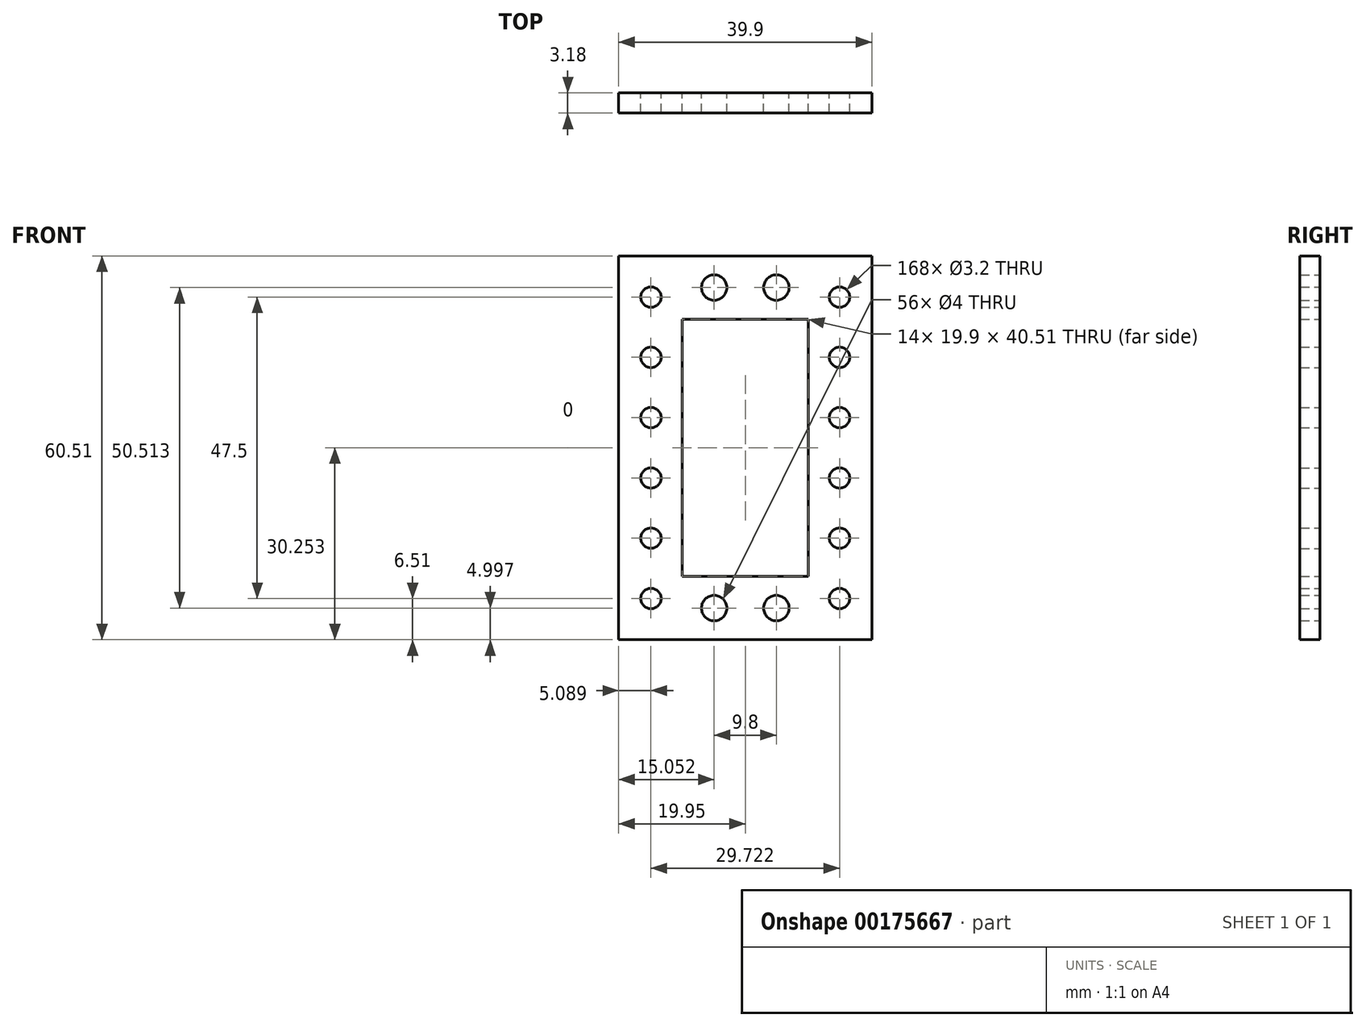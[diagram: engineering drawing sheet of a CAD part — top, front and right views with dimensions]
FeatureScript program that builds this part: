
annotation { "Feature Type Name" : "Feature", "Feature Type Description" : "" }
export const myFeature = defineFeature(function(context is Context, id is Id, definition is map)
    precondition{}
    {
        {
            var Q0;
            Q0=qCreatedBy(makeId("Front.planeOp"),FACE);
            var sketch = newSketch(context, id + "F0", { "sketchPlane" : qUnion([Q0])});
            skLineSegment(sketch, "E0.bottom", {"start": v(0, 0) * mm, "end": v(19.9, 0) * mm});
            skLineSegment(sketch, "E0.top", {"start": v(0, -40.51) * mm, "end": v(19.9, -40.51) * mm});
            skLineSegment(sketch, "E0.left", {"start": v(0, 0) * mm, "end": v(0, -40.51) * mm});
            skLineSegment(sketch, "E0.right", {"start": v(19.9, 0) * mm, "end": v(19.9, -40.51) * mm});
            skLineSegment(sketch, "E1.bottom", {"start": v(-10, 10) * mm, "end": v(29.9, 10) * mm});
            skLineSegment(sketch, "E1.top", {"start": v(-10, -50.51) * mm, "end": v(29.9, -50.51) * mm});
            skLineSegment(sketch, "E1.left", {"start": v(-10, 10) * mm, "end": v(-10, -50.51) * mm});
            skLineSegment(sketch, "E1.right", {"start": v(29.9, 10) * mm, "end": v(29.9, -50.51) * mm});
            skCircle(sketch, "E2", {"center": v(5.05, 5) * mm, "radius": 2 * mm});
            skCircle(sketch, "E3", {"center": v(14.85, 5) * mm, "radius": 2 * mm});
            skCircle(sketch, "E4.MirrorC", {"center": v(5.05, -45.51) * mm, "radius": 2 * mm});
            skCircle(sketch, "E5.MirrorC", {"center": v(14.85, -45.51) * mm, "radius": 2 * mm});
            skCircle(sketch, "E6", {"center": v(-4.91, 3.5) * mm, "radius": 1.6 * mm});
            skCircle(sketch, "E7.0.1.0", {"center": v(-4.91, -6) * mm, "radius": 1.6 * mm});
            skCircle(sketch, "E7.0.2.0", {"center": v(-4.91, -15.5) * mm, "radius": 1.6 * mm});
            skCircle(sketch, "E7.0.3.0", {"center": v(-4.91, -25) * mm, "radius": 1.6 * mm});
            skCircle(sketch, "E7.0.4.0", {"center": v(-4.91, -34.5) * mm, "radius": 1.6 * mm});
            skCircle(sketch, "E7.0.5.0", {"center": v(-4.91, -44) * mm, "radius": 1.6 * mm});
            skCircle(sketch, "E8.MirrorC", {"center": v(24.81, 3.5) * mm, "radius": 1.6 * mm});
            skCircle(sketch, "E9.MirrorC", {"center": v(24.81, -6) * mm, "radius": 1.6 * mm});
            skCircle(sketch, "E10.MirrorC", {"center": v(24.81, -15.5) * mm, "radius": 1.6 * mm});
            skCircle(sketch, "E11.MirrorC", {"center": v(24.81, -25) * mm, "radius": 1.6 * mm});
            skCircle(sketch, "E12.MirrorC", {"center": v(24.81, -34.5) * mm, "radius": 1.6 * mm});
            skCircle(sketch, "E13.MirrorC", {"center": v(24.81, -44) * mm, "radius": 1.6 * mm});
            skSolve(sketch);
        }
        {
            var Q0;
            Q0=makeQuery(id+"F0.imprint","IMPRINT",FACE,{"disambiguationData":[TD([[makeQuery(id+"F0.imprint","IMPRINT",EDGE,{"derivedFrom":sQuery(id+"F0.wireOp",EDGE,"E0.bottom")}),1.0]])]});
            extrude(context, id + "F1", {"entities" : qUnion([Q0]), "depth" : 3.17 * mm});
        }
    });
